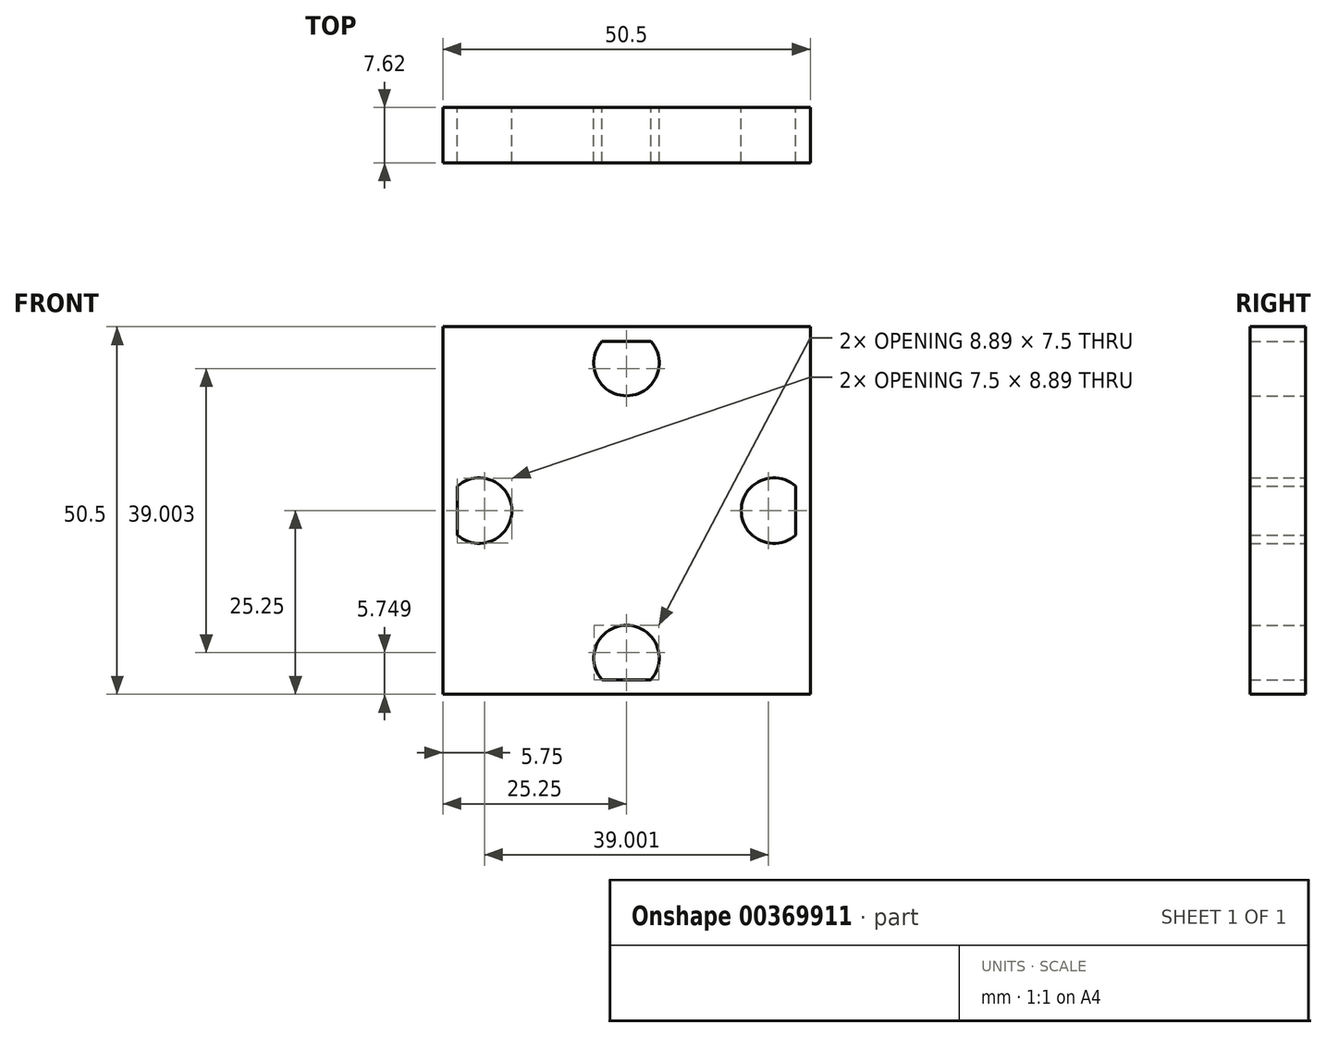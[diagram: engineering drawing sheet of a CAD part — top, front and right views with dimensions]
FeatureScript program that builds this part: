
annotation { "Feature Type Name" : "Feature", "Feature Type Description" : "" }
export const myFeature = defineFeature(function(context is Context, id is Id, definition is map)
    precondition{}
    {
        {
            var Q0;
            Q0=qCreatedBy(makeId("Front.planeOp"),FACE);
            var sketch = newSketch(context, id + "F0", { "sketchPlane" : qUnion([Q0])});
            skLineSegment(sketch, "E0.bottom", {"start": v(-25.25, 25.25) * mm, "end": v(25.25, 25.25) * mm});
            skLineSegment(sketch, "E0.top", {"start": v(-25.25, -25.25) * mm, "end": v(25.25, -25.25) * mm});
            skLineSegment(sketch, "E0.left", {"start": v(-25.25, 25.25) * mm, "end": v(-25.25, -25.25) * mm});
            skLineSegment(sketch, "E0.right", {"start": v(25.25, 25.25) * mm, "end": v(25.25, -25.25) * mm});
            skPoint(sketch, "E0.middle", {"position": v(0, 0) * mm});
            skLineSegment(sketch, "E1.bottom", {"start": v(-23.25, 23.25) * mm, "end": v(23.25, 23.25) * mm});
            skLineSegment(sketch, "E1.top", {"start": v(-23.25, -23.25) * mm, "end": v(23.25, -23.25) * mm});
            skLineSegment(sketch, "E1.left", {"start": v(-23.25, 23.25) * mm, "end": v(-23.25, -23.25) * mm});
            skLineSegment(sketch, "E1.right", {"start": v(23.25, 23.25) * mm, "end": v(23.25, -23.25) * mm});
            skCircle(sketch, "E2", {"center": v(-20.25, 0) * mm, "radius": 4.5 * mm});
            skCircle(sketch, "E3", {"center": v(0, 20.25) * mm, "radius": 4.5 * mm});
            skCircle(sketch, "E4", {"center": v(0, -20.25) * mm, "radius": 4.5 * mm});
            skCircle(sketch, "E5", {"center": v(20.25, 0) * mm, "radius": 4.5 * mm});
            skSolve(sketch);
        }
        {
            var Q0;
            {var subQ1=sQuery(id+"F0.wireOp",EDGE,"E1.bottom");var subQ8=sQuery(id+"F0.wireOp",EDGE,"E1.left");var subQ13=makeQuery(id+"F0.imprint","INTERSECT",VERTEX,{"derivedFrom":[subQ1,subQ8]});Q0=makeQuery(id+"F0.imprint","IMPRINT",FACE,{"disambiguationData":[TD([[makeQuery(id+"F0.imprint","IMPRINT",EDGE,{"disambiguationData":[TD([[subQ13,-1.0]])],"derivedFrom":subQ1}),-1.0]])]});}
            var Q1;
            {var subQ0=sQuery(id+"F0.wireOp",EDGE,"E3");var subQ1=sQuery(id+"F0.wireOp",EDGE,"E1.bottom");var subQ2=makeQuery(id+"F0.imprint","INTERSECT",VERTEX,{"disambiguationData":[OD(0.0)],"derivedFrom":[subQ1,subQ0]});Q1=makeQuery(id+"F0.imprint","IMPRINT",FACE,{"disambiguationData":[TD([[makeQuery(id+"F0.imprint","IMPRINT",EDGE,{"disambiguationData":[TD([[subQ2,-1.0]])],"derivedFrom":subQ1}),1.0]])]});}
            var Q2;
            {var subQ0=sQuery(id+"F0.wireOp",EDGE,"E3");var subQ1=sQuery(id+"F0.wireOp",EDGE,"E1.bottom");var subQ2=makeQuery(id+"F0.imprint","INTERSECT",VERTEX,{"disambiguationData":[OD(0.0)],"derivedFrom":[subQ1,subQ0]});Q2=makeQuery(id+"F0.imprint","IMPRINT",FACE,{"disambiguationData":[TD([[makeQuery(id+"F0.imprint","IMPRINT",EDGE,{"disambiguationData":[TD([[subQ2,-1.0]])],"derivedFrom":subQ1}),-1.0]])]});}
            var Q3;
            {var subQ0=sQuery(id+"F0.wireOp",EDGE,"E2");var subQ1=sQuery(id+"F0.wireOp",EDGE,"E1.left");var subQ2=makeQuery(id+"F0.imprint","INTERSECT",VERTEX,{"disambiguationData":[OD(0.0)],"derivedFrom":[subQ1,subQ0]});Q3=makeQuery(id+"F0.imprint","IMPRINT",FACE,{"disambiguationData":[TD([[makeQuery(id+"F0.imprint","IMPRINT",EDGE,{"disambiguationData":[TD([[subQ2,-1.0]])],"derivedFrom":subQ1}),1.0]])]});}
            var Q4;
            {var subQ0=sQuery(id+"F0.wireOp",EDGE,"E2");var subQ1=sQuery(id+"F0.wireOp",EDGE,"E1.left");var subQ2=makeQuery(id+"F0.imprint","INTERSECT",VERTEX,{"disambiguationData":[OD(0.0)],"derivedFrom":[subQ1,subQ0]});Q4=makeQuery(id+"F0.imprint","IMPRINT",FACE,{"disambiguationData":[TD([[makeQuery(id+"F0.imprint","IMPRINT",EDGE,{"disambiguationData":[TD([[subQ2,-1.0]])],"derivedFrom":subQ1}),-1.0]])]});}
            var Q5;
            {var subQ0=sQuery(id+"F0.wireOp",EDGE,"E4");var subQ1=sQuery(id+"F0.wireOp",EDGE,"E1.top");var subQ2=makeQuery(id+"F0.imprint","INTERSECT",VERTEX,{"disambiguationData":[OD(0.0)],"derivedFrom":[subQ1,subQ0]});Q5=makeQuery(id+"F0.imprint","IMPRINT",FACE,{"disambiguationData":[TD([[makeQuery(id+"F0.imprint","IMPRINT",EDGE,{"disambiguationData":[TD([[subQ2,-1.0]])],"derivedFrom":subQ1}),1.0]])]});}
            var Q6;
            {var subQ0=sQuery(id+"F0.wireOp",EDGE,"E4");var subQ1=sQuery(id+"F0.wireOp",EDGE,"E1.top");var subQ2=makeQuery(id+"F0.imprint","INTERSECT",VERTEX,{"disambiguationData":[OD(0.0)],"derivedFrom":[subQ1,subQ0]});Q6=makeQuery(id+"F0.imprint","IMPRINT",FACE,{"disambiguationData":[TD([[makeQuery(id+"F0.imprint","IMPRINT",EDGE,{"disambiguationData":[TD([[subQ2,-1.0]])],"derivedFrom":subQ1}),-1.0]])]});}
            var Q7;
            {var subQ0=sQuery(id+"F0.wireOp",EDGE,"E5");var subQ1=sQuery(id+"F0.wireOp",EDGE,"E1.right");var subQ2=makeQuery(id+"F0.imprint","INTERSECT",VERTEX,{"disambiguationData":[OD(0.0)],"derivedFrom":[subQ1,subQ0]});Q7=makeQuery(id+"F0.imprint","IMPRINT",FACE,{"disambiguationData":[TD([[makeQuery(id+"F0.imprint","IMPRINT",EDGE,{"disambiguationData":[TD([[subQ2,-1.0]])],"derivedFrom":subQ1}),-1.0]])]});}
            var Q8;
            {var subQ0=sQuery(id+"F0.wireOp",EDGE,"E5");var subQ1=sQuery(id+"F0.wireOp",EDGE,"E1.right");var subQ2=makeQuery(id+"F0.imprint","INTERSECT",VERTEX,{"disambiguationData":[OD(0.0)],"derivedFrom":[subQ1,subQ0]});Q8=makeQuery(id+"F0.imprint","IMPRINT",FACE,{"disambiguationData":[TD([[makeQuery(id+"F0.imprint","IMPRINT",EDGE,{"disambiguationData":[TD([[subQ2,-1.0]])],"derivedFrom":subQ1}),1.0]])]});}
            var Q9;
            {var subQ1=sQuery(id+"F0.wireOp",EDGE,"E1.top");var subQ6=sQuery(id+"F0.wireOp",EDGE,"E1.left");var subQ10=makeQuery(id+"F0.imprint","INTERSECT",VERTEX,{"derivedFrom":[subQ1,subQ6]});Q9=makeQuery(id+"F0.imprint","IMPRINT",FACE,{"disambiguationData":[TD([[makeQuery(id+"F0.imprint","IMPRINT",EDGE,{"disambiguationData":[TD([[subQ10,-1.0]])],"derivedFrom":subQ1}),1.0]])]});}
            var Q10;
            {var subQ1=sQuery(id+"F0.wireOp",EDGE,"E1.top");var subQ6=sQuery(id+"F0.wireOp",EDGE,"E1.right");var subQ10=makeQuery(id+"F0.imprint","INTERSECT",VERTEX,{"derivedFrom":[subQ1,subQ6]});Q10=makeQuery(id+"F0.imprint","IMPRINT",FACE,{"disambiguationData":[TD([[makeQuery(id+"F0.imprint","IMPRINT",EDGE,{"disambiguationData":[TD([[subQ10,1.0]])],"derivedFrom":subQ1}),1.0]])]});}
            var Q11;
            {var subQ1=sQuery(id+"F0.wireOp",EDGE,"E1.right");var subQ5=sQuery(id+"F0.wireOp",EDGE,"E1.bottom");var subQ6=makeQuery(id+"F0.imprint","INTERSECT",VERTEX,{"derivedFrom":[subQ5,subQ1]});Q11=makeQuery(id+"F0.imprint","IMPRINT",FACE,{"disambiguationData":[TD([[makeQuery(id+"F0.imprint","IMPRINT",EDGE,{"disambiguationData":[TD([[subQ6,1.0]])],"derivedFrom":subQ5}),-1.0]])]});}
            var Q12;
            {var subQ0=sQuery(id+"F0.wireOp",EDGE,"1ad9F6E1-xDbz-jqtR-eg6b-pqv92Zdiw2X0.left");var subQ3=sQuery(id+"F0.wireOp",EDGE,"E2");var subQ4=makeQuery(id+"F0.imprint","INTERSECT",VERTEX,{"disambiguationData":[OD(0.0)],"derivedFrom":[subQ3,subQ0]});Q12=makeQuery(id+"F0.imprint","IMPRINT",FACE,{"disambiguationData":[TD([[makeQuery(id+"F0.imprint","IMPRINT",EDGE,{"disambiguationData":[TD([[subQ4,1.0]])],"derivedFrom":subQ3}),-1.0]])]});}
            var Q13;
            {var subQ0=sQuery(id+"F0.wireOp",EDGE,"1ad9F6E1-xDbz-jqtR-eg6b-pqv92Zdiw2X0.left");var subQ1=sQuery(id+"F0.wireOp",EDGE,"E2");var subQ2=makeQuery(id+"F0.imprint","INTERSECT",VERTEX,{"disambiguationData":[OD(0.0)],"derivedFrom":[subQ1,subQ0]});Q13=makeQuery(id+"F0.imprint","IMPRINT",FACE,{"disambiguationData":[TD([[makeQuery(id+"F0.imprint","IMPRINT",EDGE,{"disambiguationData":[TD([[subQ2,1.0]])],"derivedFrom":subQ1}),1.0]])]});}
            var Q14;
            {var subQ0=sQuery(id+"F0.wireOp",EDGE,"1ad9F6E1-xDbz-jqtR-eg6b-pqv92Zdiw2X0.bottom");var subQ1=sQuery(id+"F0.wireOp",EDGE,"E3");var subQ2=makeQuery(id+"F0.imprint","INTERSECT",VERTEX,{"disambiguationData":[OD(0.0)],"derivedFrom":[subQ1,subQ0]});Q14=makeQuery(id+"F0.imprint","IMPRINT",FACE,{"disambiguationData":[TD([[makeQuery(id+"F0.imprint","IMPRINT",EDGE,{"disambiguationData":[TD([[subQ2,-1.0]])],"derivedFrom":subQ1}),1.0]])]});}
            var Q15;
            {var subQ0=sQuery(id+"F0.wireOp",EDGE,"1ad9F6E1-xDbz-jqtR-eg6b-pqv92Zdiw2X0.right");var subQ1=sQuery(id+"F0.wireOp",EDGE,"E5");var subQ2=makeQuery(id+"F0.imprint","INTERSECT",VERTEX,{"disambiguationData":[OD(0.0)],"derivedFrom":[subQ1,subQ0]});Q15=makeQuery(id+"F0.imprint","IMPRINT",FACE,{"disambiguationData":[TD([[makeQuery(id+"F0.imprint","IMPRINT",EDGE,{"disambiguationData":[TD([[subQ2,-1.0]])],"derivedFrom":subQ1}),1.0]])]});}
            var Q16;
            {var subQ0=sQuery(id+"F0.wireOp",EDGE,"1ad9F6E1-xDbz-jqtR-eg6b-pqv92Zdiw2X0.top");var subQ1=sQuery(id+"F0.wireOp",EDGE,"E4");var subQ2=makeQuery(id+"F0.imprint","INTERSECT",VERTEX,{"disambiguationData":[OD(0.0)],"derivedFrom":[subQ1,subQ0]});Q16=makeQuery(id+"F0.imprint","IMPRINT",FACE,{"disambiguationData":[TD([[makeQuery(id+"F0.imprint","IMPRINT",EDGE,{"disambiguationData":[TD([[subQ2,1.0]])],"derivedFrom":subQ1}),1.0]])]});}
            extrude(context, id + "F1", {"entities" : qUnion([Q0, Q1, Q2, Q3, Q4, Q5, Q6, Q7, Q8, Q9, Q10, Q11, Q12, Q13, Q14, Q15, Q16]), "depth" : 7.62 * mm});
        }
        {
            var Q0;
            Q0 = qSketchRegion(id + "F0", true);
            extrude(context, id + "F2", {"entities" : qUnion([Q0]), "operationType" : NewBodyOperationType.ADD, "depth" : 2.54 * mm});
        }
        {
            var Q0;
            Q0=makeQuery(id+"F1.opExtrude","CAP_FACE",FACE,{"disambiguationData":[OSD([sQuery(id+"F0.wireOp",EDGE,"E1.bottom"),sQuery(id+"F0.wireOp",EDGE,"E1.top"),sQuery(id+"F0.wireOp",EDGE,"E1.left"),sQuery(id+"F0.wireOp",EDGE,"E1.right"),sQuery(id+"F0.wireOp",EDGE,"E2"),sQuery(id+"F0.wireOp",EDGE,"E3"),sQuery(id+"F0.wireOp",EDGE,"E4"),sQuery(id+"F0.wireOp",EDGE,"E5")])],"isStart":false});
            var sketch = newSketch(context, id + "F3", { "sketchPlane" : qUnion([Q0])});
            skLineSegment(sketch, "E6.bottom", {"start": v(-19.05, 19.05) * mm, "end": v(19.05, 19.05) * mm});
            skLineSegment(sketch, "E6.top", {"start": v(-19.05, -19.05) * mm, "end": v(19.05, -19.05) * mm});
            skLineSegment(sketch, "E6.left", {"start": v(-19.05, 19.05) * mm, "end": v(-19.05, -19.05) * mm});
            skLineSegment(sketch, "E6.right", {"start": v(19.05, 19.05) * mm, "end": v(19.05, -19.05) * mm});
            skPoint(sketch, "E6.middle", {"position": v(0, 0) * mm});
            skSolve(sketch);
        }
        {
            var Q0;
            Q0=makeQuery(id+"F3.imprint","IMPRINT",FACE,{"disambiguationData":[TD([[makeQuery(id+"F3.imprint","IMPRINT",EDGE,{"derivedFrom":sQuery(id+"F3.wireOp",EDGE,"E6.bottom")}),-1.0]])]});
            extrude(context, id + "F4", {"entities" : qUnion([Q0]), "operationType" : NewBodyOperationType.REMOVE, "oppositeDirection" : true, "depth" : 5.08 * mm});
        }
    });
